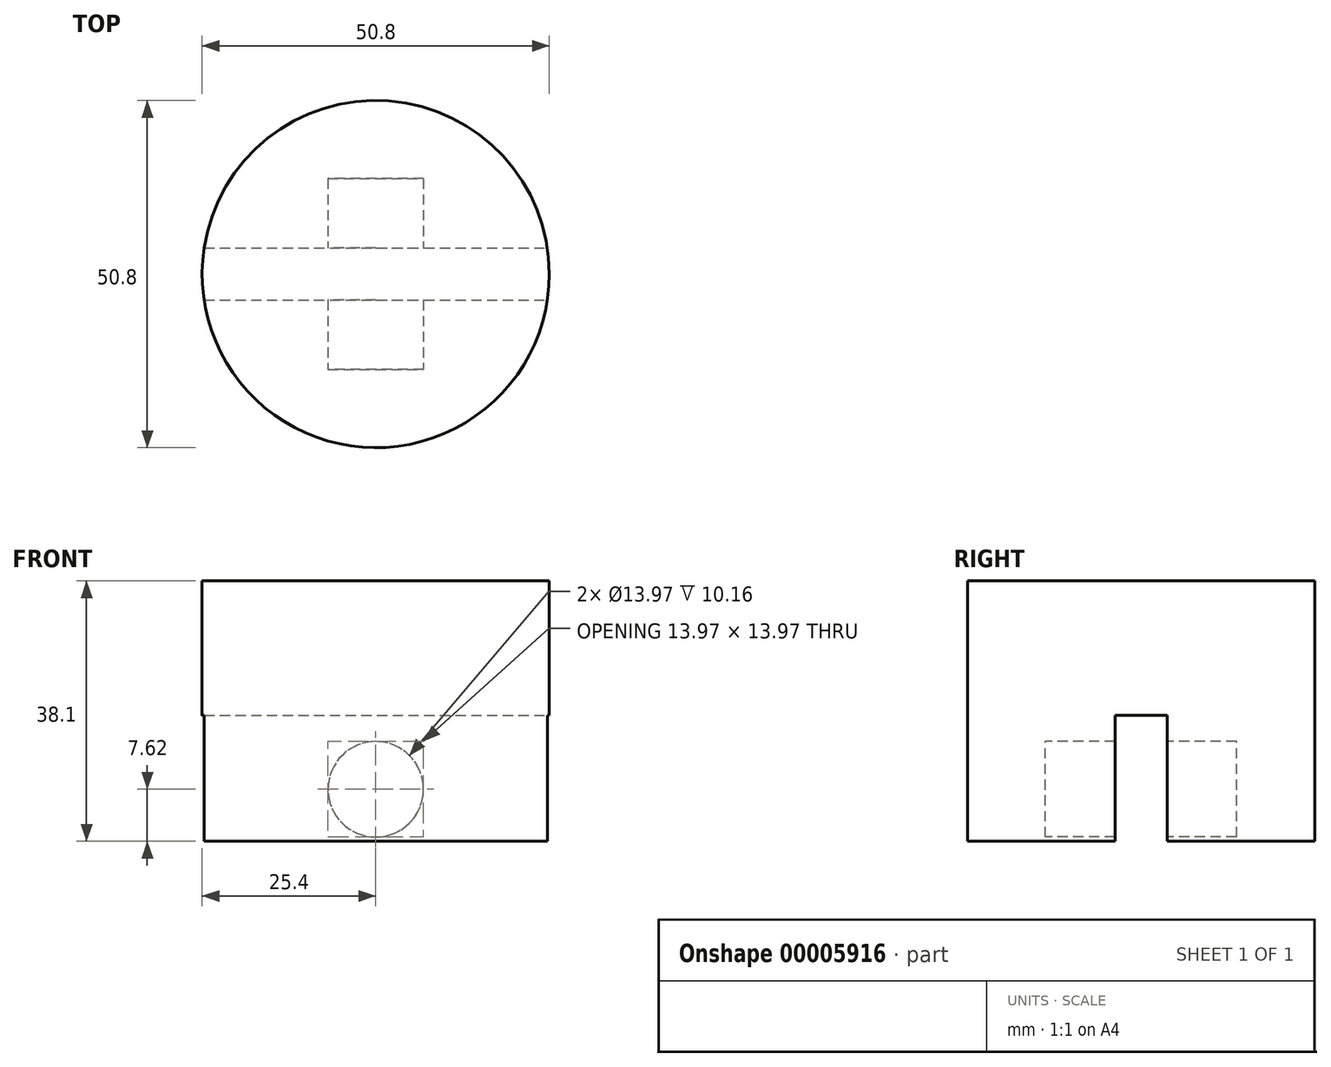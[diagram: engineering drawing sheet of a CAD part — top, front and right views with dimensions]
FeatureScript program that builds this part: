
annotation { "Feature Type Name" : "Feature", "Feature Type Description" : "" }
export const myFeature = defineFeature(function(context is Context, id is Id, definition is map)
    precondition{}
    {
        {
            var Q0;
            Q0=qCreatedBy(makeId("Top.planeOp"),FACE);
            var sketch = newSketch(context, id + "F0", { "sketchPlane" : qUnion([Q0])});
            skCircle(sketch, "E0", {"center": v(0, 0) * mm, "radius": 25.4 * mm});
            skSolve(sketch);
        }
        {
            var Q0;
            Q0 = qSketchRegion(id + "F0", true);
            extrude(context, id + "F1", {"entities" : qUnion([Q0]), "depth" : 38.1 * mm});
        }
        {
            var Q0;
            Q0=qCreatedBy(makeId("Right.planeOp"),FACE);
            var sketch = newSketch(context, id + "F2", { "sketchPlane" : qUnion([Q0])});
            skLineSegment(sketch, "E1.0", {"start": v(-25.4, 0) * mm, "end": v(25.4, 0) * mm, "construction": true});
            skLineSegment(sketch, "E2", {"start": v(0, 0) * mm, "end": v(0, 18.41) * mm, "construction": true});
            skLineSegment(sketch, "E3.rect.bottom", {"start": v(-3.81, 0) * mm, "end": v(3.81, 0) * mm});
            skLineSegment(sketch, "E3.rect.top", {"start": v(-3.8, 18.41) * mm, "end": v(3.81, 18.41) * mm});
            skLineSegment(sketch, "E3.rect.left", {"start": v(-3.81, 0) * mm, "end": v(-3.8, 18.41) * mm});
            skLineSegment(sketch, "E3.rect.right", {"start": v(3.8, 0) * mm, "end": v(3.81, 18.41) * mm});
            skPoint(sketch, "E3.rect.middle", {"position": v(0, 9.2) * mm});
            skSolve(sketch);
        }
        {
            var Q0;
            Q0=qCreatedBy(makeId("Front.planeOp"),FACE);
            var sketch = newSketch(context, id + "F3", { "sketchPlane" : qUnion([Q0])});
            skLineSegment(sketch, "E4", {"start": v(0, 0) * mm, "end": v(0, 7.62) * mm, "construction": true});
            skCircle(sketch, "E5", {"center": v(0, 7.62) * mm, "radius": 6.99 * mm});
            skSolve(sketch);
        }
        {
            var Q0;
            Q0 = qSketchRegion(id + "F2", true);
            extrude(context, id + "F4", {"entities" : qUnion([Q0]), "operationType" : NewBodyOperationType.REMOVE, "endBound" : BoundingType.SYMMETRIC, "oppositeDirection" : true, "depth" : 127 * mm});
        }
        {
            var Q0;
            Q0 = qSketchRegion(id + "F3", true);
            extrude(context, id + "F5", {"entities" : qUnion([Q0]), "operationType" : NewBodyOperationType.REMOVE, "endBound" : BoundingType.SYMMETRIC, "oppositeDirection" : true, "depth" : 27.94 * mm});
        }
    });
